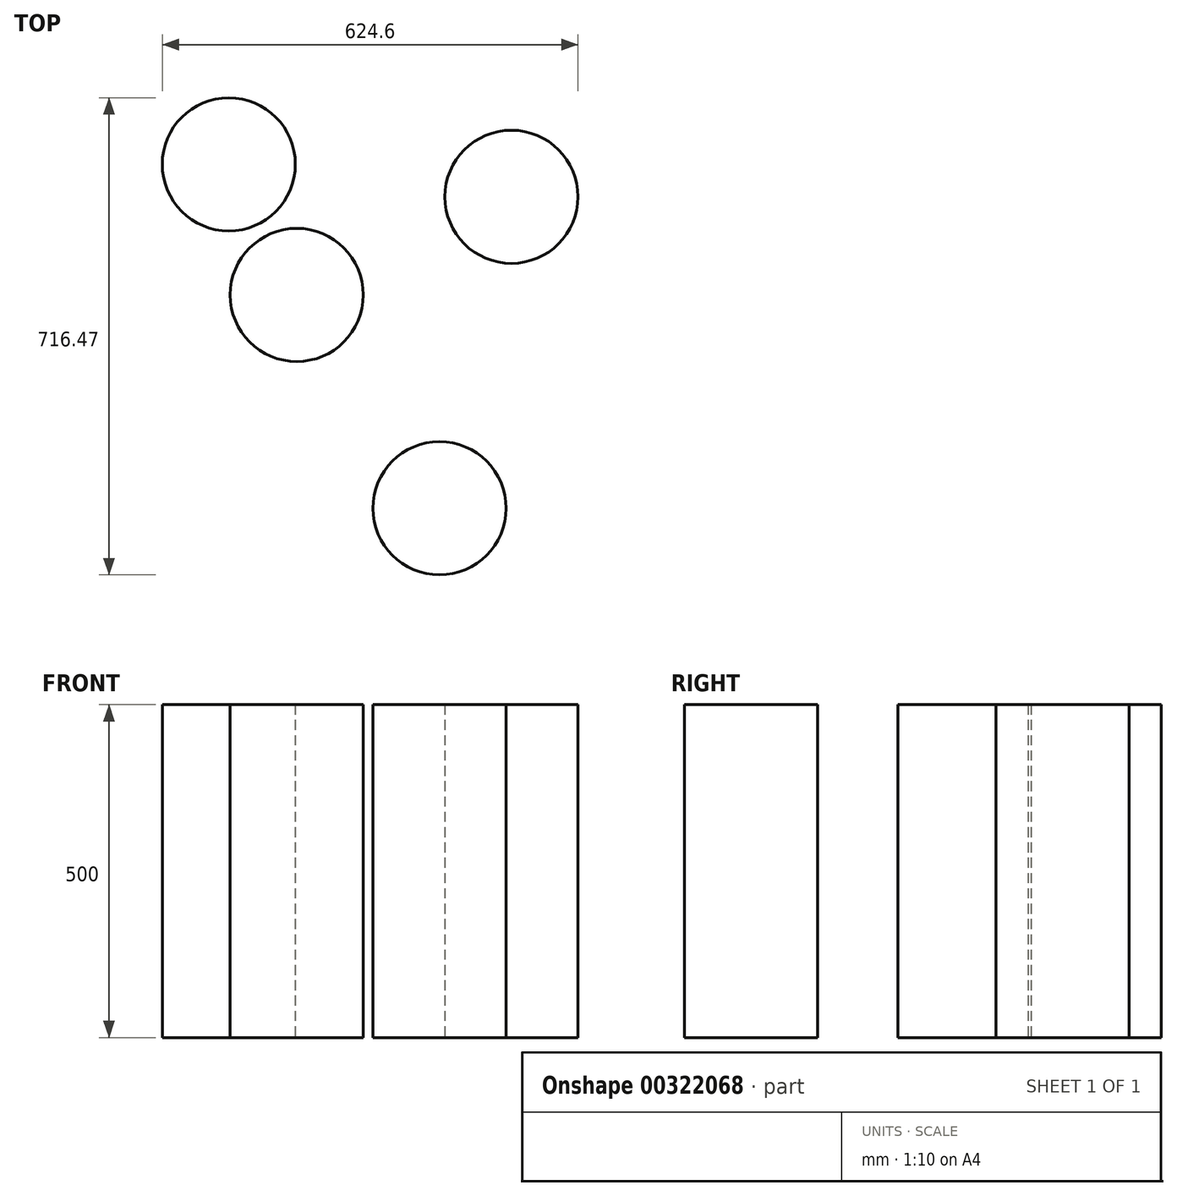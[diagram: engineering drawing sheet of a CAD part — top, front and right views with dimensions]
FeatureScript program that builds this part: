
annotation { "Feature Type Name" : "Feature", "Feature Type Description" : "" }
export const myFeature = defineFeature(function(context is Context, id is Id, definition is map)
    precondition{}
    {
        {
            var Q0;
            Q0=qCreatedBy(makeId("Top.planeOp"),FACE);
            var sketch = newSketch(context, id + "F0", { "sketchPlane" : qUnion([Q0])});
            skCircle(sketch, "E0", {"center": v(-266.33, 228.95) * mm, "radius": 100 * mm});
            skCircle(sketch, "E1", {"center": v(-164.3, 32.83) * mm, "radius": 100 * mm});
            skCircle(sketch, "E2", {"center": v(50.23, -287.52) * mm, "radius": 100 * mm});
            skCircle(sketch, "E3", {"center": v(158.27, 180.23) * mm, "radius": 100 * mm});
            skSolve(sketch);
        }
        {
            var Q0;
            Q0 = qSketchRegion(id + "F0", true);
            extrude(context, id + "F1", {"entities" : qUnion([Q0]), "depth" : 500 * mm});
        }
    });
